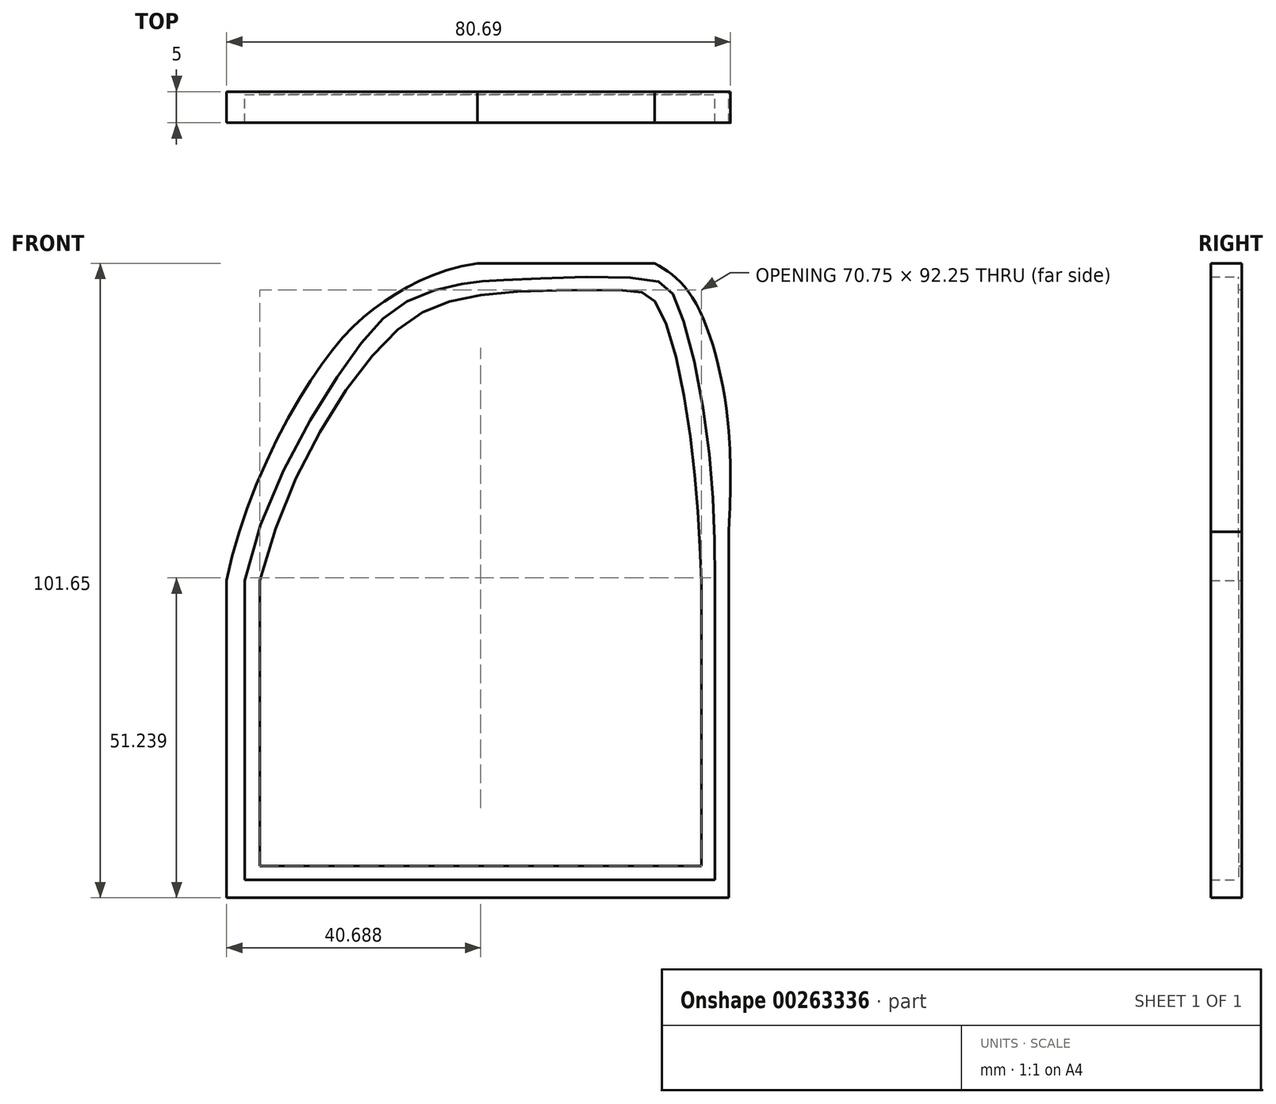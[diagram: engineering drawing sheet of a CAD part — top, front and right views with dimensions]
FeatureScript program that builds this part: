
annotation { "Feature Type Name" : "Feature", "Feature Type Description" : "" }
export const myFeature = defineFeature(function(context is Context, id is Id, definition is map)
    precondition{}
    {
        {
            var Q0;
            Q0=qCreatedBy(makeId("Front.planeOp"),FACE);
            var sketch = newSketch(context, id + "F0", { "sketchPlane" : qUnion([Q0])});
            skLineSegment(sketch, "E0.bottom", {"start": v(-6.38, 46.5) * mm, "end": v(21.95, 46.5) * mm});
            skLineSegment(sketch, "E0.top", {"start": v(-46.59, -55.14) * mm, "end": v(33.83, -55.14) * mm});
            skLineSegment(sketch, "E0.left", {"start": v(-46.59, -4.32) * mm, "end": v(-46.59, -55.14) * mm});
            skLineSegment(sketch, "E0.right", {"start": v(33.83, 19.6) * mm, "end": v(33.83, -55.14) * mm});
            skFitSpline(sketch, "E1", {"points": [v(-46.59, -4.32) * mm, v(-30.87, 31) * mm, v(-20.25, 41.13) * mm, v(-6.38, 46.5) * mm], "startDerivative": vector(17.33, 88.44) * mm, "endDerivative": vector(60.56, 8.43) * mm});
            skPoint(sketch, "E2.orphan", {"position": v(-46.59, 46.5) * mm});
            skFitSpline(sketch, "E3", {"points": [v(21.95, 46.5) * mm, v(27.63, 41.64) * mm, v(33.83, 19.6) * mm, v(33.83, 3.49) * mm, v(33.83, 3.37) * mm], "startDerivative": vector(25.35, -15.2) * mm, "endDerivative": vector(0.18, -3.1) * mm});
            skPoint(sketch, "E4.orphan", {"position": v(33.83, 46.5) * mm});
            skLineSegment(sketch, "E5.top", {"start": v(-43.68, -52.26) * mm, "end": v(31.62, -52.26) * mm});
            skLineSegment(sketch, "E5.left", {"start": v(-43.68, -4.32) * mm, "end": v(-43.68, -52.26) * mm});
            skLineSegment(sketch, "E5.right", {"start": v(31.62, -4.32) * mm, "end": v(31.62, -52.26) * mm});
            skFitSpline(sketch, "E6", {"points": [v(-43.68, -4.32) * mm, v(-27, 31) * mm, v(-17.27, 40.65) * mm, v(-7.5, 43.38) * mm, v(-1.6, 43.84) * mm, v(20.74, 44) * mm, v(25.12, 41.13) * mm, v(30.28, 19.6) * mm, v(31.62, -4.32) * mm], "startDerivative": vector(40.76, 206.76) * mm, "endDerivative": vector(0.55, -146.46) * mm});
            skLineSegment(sketch, "E7.top", {"start": v(-41.28, -50.03) * mm, "end": v(29.47, -50.03) * mm});
            skLineSegment(sketch, "E7.left", {"start": v(-41.28, -4.32) * mm, "end": v(-41.28, -50.03) * mm});
            skLineSegment(sketch, "E7.right", {"start": v(29.47, -4.32) * mm, "end": v(29.47, -50.03) * mm});
            skFitSpline(sketch, "E8", {"points": [v(29.47, -4.32) * mm, v(27.6, 19.6) * mm, v(21.96, 40.45) * mm, v(16.9, 42.14) * mm, v(-5.95, 41.4) * mm, v(-20.95, 34.2) * mm, v(-41.28, -4.32) * mm], "startDerivative": vector(-5.83, 122.07) * mm, "endDerivative": vector(-47.07, -192.85) * mm});
            skSolve(sketch);
        }
        {
            var Q0;
            Q0=qSketchRegion(id+"F0",true);
            extrude(context, id + "F1", {"entities" : qUnion([Q0]), "depth" : 5 * mm});
        }
        {
            var Q0;
            Q0=makeQuery(id+"F0.imprint","IMPRINT",FACE,{"disambiguationData":[TD([[makeQuery(id+"F0.imprint","IMPRINT",EDGE,{"derivedFrom":sQuery(id+"F0.wireOp",EDGE,"E5.top")}),1.0]])]});
            extrude(context, id + "F2", {"entities" : qUnion([Q0]), "operationType" : NewBodyOperationType.ADD, "depth" : 0.5 * mm});
        }
    });
